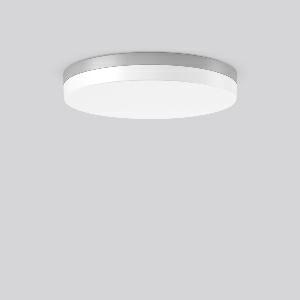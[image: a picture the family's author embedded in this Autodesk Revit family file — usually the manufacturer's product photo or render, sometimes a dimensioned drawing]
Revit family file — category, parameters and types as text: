
# Revit family: flat_slim_round_312634_004_1_76_f295
name_source: partatom
category: Lighting Fixtures
units: mm (PartAtom-declared; Revit-internal decimal feet)

## family parameters
Cut with Voids When Loaded = No
Host = Face
Light Source = No
Part Type = Normal
Room Calculation Point = No
Round Connector Dimension = Use Diameter
Shared = No

## types (1)
- MultiLumen 1 830 (1 x LED Modul 830, 3500 lm, 3000)
    Apparent Load = 24 VA
    CIE Flux Codes = 38 68 89 85 100
    Color Rendering = 80
    Color Temperature = 3000
    Default Elevation = 1800 mm
    Height = 70 mm
    Lamp = 1 x LED Modul 830
    Lamp Light Flux = 3500 lm
    Lamp count = 1
    Length = 480 mm
    Lifetime = 50000 h
    Luminous efficacy = 146 lm/W
    Manufacturer = RZB
    ModVariant = No
    Model = 312634.004.1.76
    Mounting Place = Ceiling
    Mounting Type = Surface mounted
    Number of Poles = 1
    OnlyDefault = Yes
    Power Factor = 1
    Product Name = FLAT SLIM round
    Product group = Surface mounted ceiling and wall luminaires
    ProductGroupID = 305
    Protection Class = Protection class I
    Protection Degree = Degree of protection
    RLX_Detail_Level = 1
    RLX_Emergency_Light_Flux = 0 lm
    RLX_Emergency_Type = 0
    RLX_Emergency_Type_DB = No
    RlxData = <blob elided: 21713 chars, md5=4d42b515>
    Socket = socket
    Standby Power = 0 W
    System Light Flux = 3500 lm
    System Power = 24 W
    Type Comments = MultiLumen 1 830
    Type Image = 312633.004.jpg
    URL = http://relux.com
    VarID = multilumen_1_830
    Voltage = 0 V
    Weight = 0.00 kg
    Width = 0 mm  [stored 0 ft]

note: [stored X ft] marks values corroborated as IEEE doubles in the binary element streams (Revit-internal decimal feet)

## geometry (parser evidence)
native form markers: Blend x4, Sweep x14
no freeform markers — native parametric forms only
